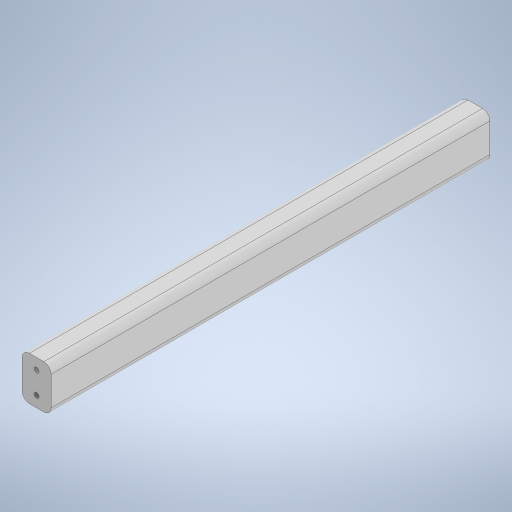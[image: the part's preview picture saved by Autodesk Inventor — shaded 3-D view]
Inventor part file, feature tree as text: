
AUTODESK INVENTOR PART (.ipt)
format: ipt  version: 2023 (Build 270158000, 158)  size: 260,096 bytes
history: native  units: in
note: dims shown in document units (in); Inventor stores cm internally (conversion verified against a paired STEP export)
features: sketch x3, hole x2, extrude x1, fillet x1
ambient origin geometry x8: Origin, YZ Plane, XZ Plane, XY Plane, X Axis, Y Axis, Z Axis, Center Point
bodies: Solid1 (feature_tree)
feature tree (7):
  extrude  "Extrusion1"  Depth=0.75in
  sketch  "Sketch2"  dims[d4=0.112in d5=0.112in]
  sketch  "Sketch3"  dims[d18=0.125in d19=0.0849in d20=0.75in d21=0.375in d22=0.25in d23=0.5635in d24=1.0in d25=0.8108in d26=0.0849in d27=0.75in d28=0.375in d29=0.25in d30=0.5635in d31=1.0in d32=0.8108in]
  fillet  "Fillet1"  Radius=7.54in
  hole  "Hole1"  [1 undecoded]
  hole  "Hole2"  [1 undecoded]
  sketch  "Sketch1"  dims[d0=0.5in d1=0.75in d2=7.54in d3=0.0in]
note: 2 required parameter values undecoded (feature->parameter linkage not recoverable at this tier; creation-order binding heuristic only, values carry confidence <= 0.55)
